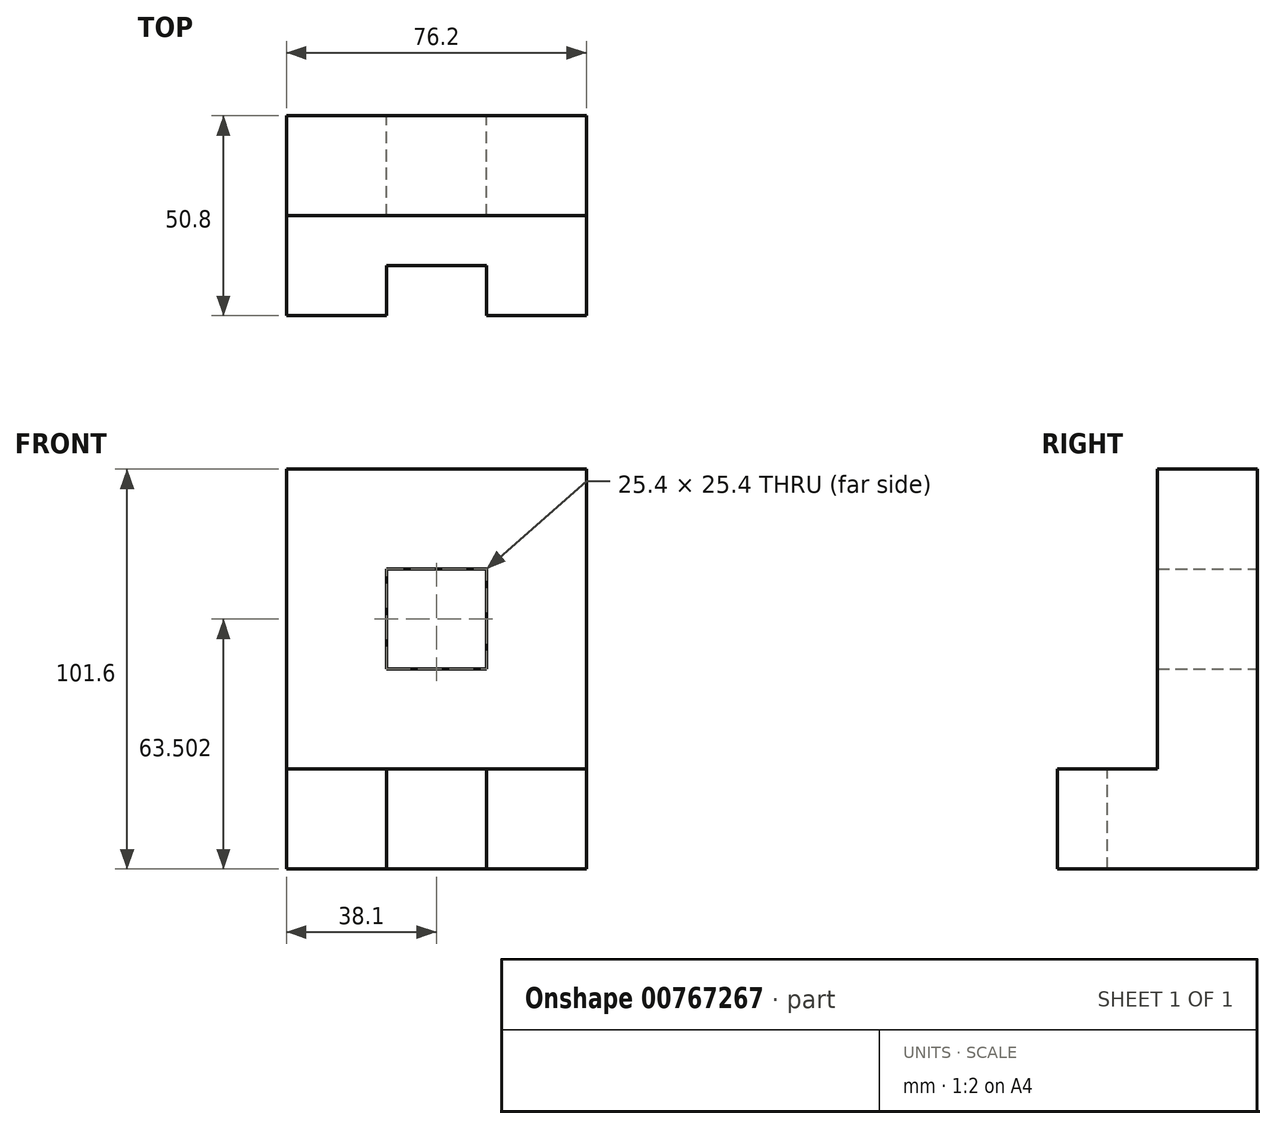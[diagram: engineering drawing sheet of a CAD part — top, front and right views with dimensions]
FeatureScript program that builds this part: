
annotation { "Feature Type Name" : "Feature", "Feature Type Description" : "" }
export const myFeature = defineFeature(function(context is Context, id is Id, definition is map)
    precondition{}
    {
        {
            var Q0;
            Q0=qCreatedBy(makeId("Front.planeOp"),FACE);
            var sketch = newSketch(context, id + "F0", { "sketchPlane" : qUnion([Q0])});
            skPoint(sketch, "E0.middle", {"position": v(0, 0) * mm});
            skLineSegment(sketch, "E1.top", {"start": v(-38.1, 75.43) * mm, "end": v(38.1, 75.43) * mm});
            skLineSegment(sketch, "E1.left", {"start": v(-38.1, -0.77) * mm, "end": v(-38.1, 75.43) * mm});
            skLineSegment(sketch, "E1.right", {"start": v(38.1, -0.77) * mm, "end": v(38.1, 75.43) * mm});
            skLineSegment(sketch, "E2", {"start": v(-38.1, -0.77) * mm, "end": v(38.1, -0.77) * mm});
            skLineSegment(sketch, "E3", {"start": v(38.1, -0.77) * mm, "end": v(38.1, -26.17) * mm});
            skLineSegment(sketch, "E4", {"start": v(38.1, -26.17) * mm, "end": v(-38.1, -26.17) * mm});
            skLineSegment(sketch, "E5", {"start": v(-38.1, -26.17) * mm, "end": v(-38.1, -0.77) * mm});
            skLineSegment(sketch, "E6", {"start": v(-12.7, -26.17) * mm, "end": v(-12.7, -0.77) * mm});
            skLineSegment(sketch, "E7", {"start": v(12.7, -26.17) * mm, "end": v(12.7, -0.77) * mm});
            skLineSegment(sketch, "E8.bottom", {"start": v(-12.7, 50.03) * mm, "end": v(12.7, 50.03) * mm});
            skLineSegment(sketch, "E8.top", {"start": v(-12.7, 24.63) * mm, "end": v(12.7, 24.63) * mm});
            skLineSegment(sketch, "E8.left", {"start": v(-12.7, 50.03) * mm, "end": v(-12.7, 24.63) * mm});
            skLineSegment(sketch, "E8.right", {"start": v(12.7, 50.03) * mm, "end": v(12.7, 24.63) * mm});
            skSolve(sketch);
        }
        {
            var Q0;
            {var subQ0=sQuery(id+"F0.wireOp",EDGE,"E5");Q0=makeQuery(id+"F0.imprint","IMPRINT",FACE,{"disambiguationData":[TD([[makeQuery(id+"F0.imprint","IMPRINT",EDGE,{"derivedFrom":subQ0}),-1.0]])]});}
            var Q1;
            {var subQ0=sQuery(id+"F0.wireOp",EDGE,"E3");Q1=makeQuery(id+"F0.imprint","IMPRINT",FACE,{"disambiguationData":[TD([[makeQuery(id+"F0.imprint","IMPRINT",EDGE,{"derivedFrom":subQ0}),-1.0]])]});}
            extrude(context, id + "F1", {"entities" : qUnion([Q0, Q1]), "depth" : 38.1 * mm, "offsetDistance" : 25.4 * mm});
        }
        {
            var Q0;
            {var subQ0=sQuery(id+"F0.wireOp",EDGE,"E3");Q0=makeQuery(id+"F0.imprint","IMPRINT",FACE,{"disambiguationData":[TD([[makeQuery(id+"F0.imprint","IMPRINT",EDGE,{"derivedFrom":subQ0}),-1.0]])]});}
            var Q1;
            {var subQ0=sQuery(id+"F0.wireOp",EDGE,"E5");Q1=makeQuery(id+"F0.imprint","IMPRINT",FACE,{"disambiguationData":[TD([[makeQuery(id+"F0.imprint","IMPRINT",EDGE,{"derivedFrom":subQ0}),-1.0]])]});}
            extrude(context, id + "F2", {"entities" : qUnion([Q0, Q1]), "operationType" : NewBodyOperationType.ADD, "oppositeDirection" : true, "depth" : 12.7 * mm, "offsetDistance" : 25.4 * mm});
        }
        {
            var Q0;
            {var subQ0=sQuery(id+"F0.wireOp",EDGE,"E6");Q0=makeQuery(id+"F0.imprint","IMPRINT",FACE,{"disambiguationData":[TD([[makeQuery(id+"F0.imprint","IMPRINT",EDGE,{"derivedFrom":subQ0}),-1.0]])]});}
            extrude(context, id + "F3", {"entities" : qUnion([Q0]), "operationType" : NewBodyOperationType.ADD, "depth" : 25.4 * mm, "offsetDistance" : 25.4 * mm});
        }
        {
            var Q0;
            {var subQ0=sQuery(id+"F0.wireOp",EDGE,"E6");Q0=makeQuery(id+"F0.imprint","IMPRINT",FACE,{"disambiguationData":[TD([[makeQuery(id+"F0.imprint","IMPRINT",EDGE,{"derivedFrom":subQ0}),-1.0]])]});}
            extrude(context, id + "F4", {"entities" : qUnion([Q0]), "operationType" : NewBodyOperationType.ADD, "oppositeDirection" : true, "depth" : 12.7 * mm, "offsetDistance" : 25.4 * mm});
        }
        {
            var Q0;
            Q0=makeQuery(id+"F0.imprint","IMPRINT",FACE,{"disambiguationData":[TD([[makeQuery(id+"F0.imprint","IMPRINT",EDGE,{"derivedFrom":sQuery(id+"F0.wireOp",EDGE,"E1.top")}),-1.0]])]});
            extrude(context, id + "F5", {"entities" : qUnion([Q0]), "operationType" : NewBodyOperationType.ADD, "endBound" : BoundingType.SYMMETRIC, "depth" : 25.4 * mm, "offsetDistance" : 25.4 * mm});
        }
    });
